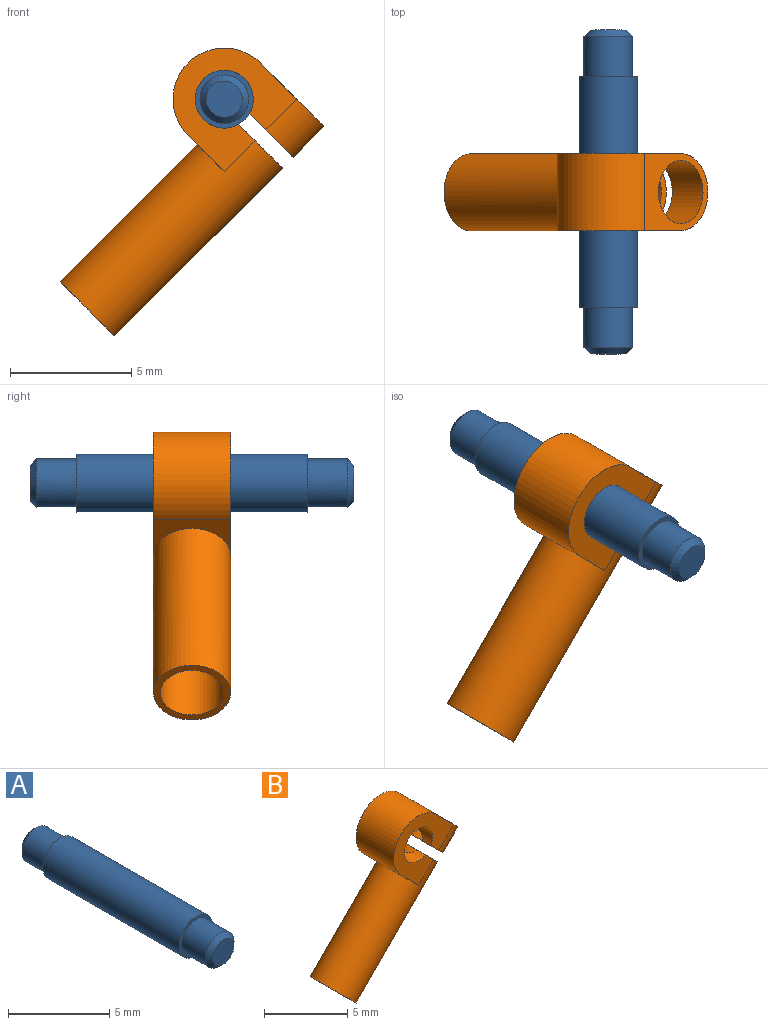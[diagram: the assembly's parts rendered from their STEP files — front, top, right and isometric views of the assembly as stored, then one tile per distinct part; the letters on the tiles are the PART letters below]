
ASSEMBLY  parts=2 mates=1
PART A: 9 faces, bbox 2.4x13.3x2.4 mm
  f0: cylinder r=1mm len=2mm, axis (0,-1,0), area 10.4mm2, adj f3,f4
  f1: plane 1.49x1.49mm, normal (0,1,0), area 1.7mm2, adj f4
  f2: cylinder r=1.19mm len=9.53mm, axis (0,-1,0), area 71.3mm2, adj f3,f7
  f3: plane 2.38x2.38mm, normal (0,1,0), area 1.3mm2, adj f0,f2
  f4: cone r=1mm half-angle=45deg, axis (0,-1,0), area 2mm2, adj f0,f1
  f5: cylinder r=1mm len=2mm, axis (0,1,0), area 10.4mm2, adj f7,f8
  f6: plane 1.49x1.49mm, normal (0,-1,0), area 1.7mm2, adj f8
  f7: plane 2.38x2.38mm, normal (0,-1,0), area 1.3mm2, adj f2,f5
  f8: cone r=1mm half-angle=45deg, axis (0,1,0), area 2mm2, adj f5,f6
PART B: 13 faces, bbox 10.9x3.2x11.9 mm
  f0: cylinder r=1.59mm len=3.18mm, axis (-0.71,0,-0.71), area 8.9mm2, adj f1,f2,f5,f10
  f1: plane 5.09x5.09mm, normal (0,-1,0), area 10.8mm2, adj f0,f4,f5,f7,f8,f10,f11,f12
  f2: plane 5.09x5.09mm, normal (0,1,0), area 10.8mm2, adj f0,f4,f5,f7,f8,f10,f11,f12
  f3: cylinder r=1.3mm len=3.1mm, axis (0.71,0,0.71), area 13.8mm2, adj f5,f10,f11
  f4: cylinder r=1.59mm len=9.15mm, axis (-0.71,0,-0.71), area 88.5mm2, adj f1,f2,f6,f8,f12
  f5: plane 3.18x2.61mm, normal (0.71,0,0.71), area 5.3mm2, adj f0,f1,f2,f3,f7
  f6: plane 3.18x2.25mm, normal (-0.71,0,-0.71), area 2.6mm2, adj f4,f9
  f7: cylinder r=2.11mm len=3.6mm, axis (0,1,0), area 21mm2, adj f1,f2,f5,f8
  f8: plane 3.18x1.49mm, normal (-0.71,0,-0.71), area 2.7mm2, adj f1,f2,f4,f7
  f9: cylinder r=1.3mm len=8.74mm, axis (0.71,0,0.71), area 79mm2, adj f6,f11,f12
  f10: plane 3.18x1.8mm, normal (-0.71,0,-0.71), area 2.1mm2, adj f0,f1,f2,f3,f11
  f11: cylinder r=1.19mm len=3.18mm, axis (0,-1,0), area 20mm2, adj f1,f2,f3,f9,f10,f12
  f12: plane 3.18x1.8mm, normal (0.71,0,0.71), area 2.1mm2, adj f1,f2,f4,f9,f11
PLACE A rot(axis=(1,0,0),180deg) t=(6.74,-46.81,74.23)mm
PLACE B at identity fixed
MATE fastened A.f0 <-> B.f7  axis (0,1,0) through (32.29,-23.41,40.48)mm
